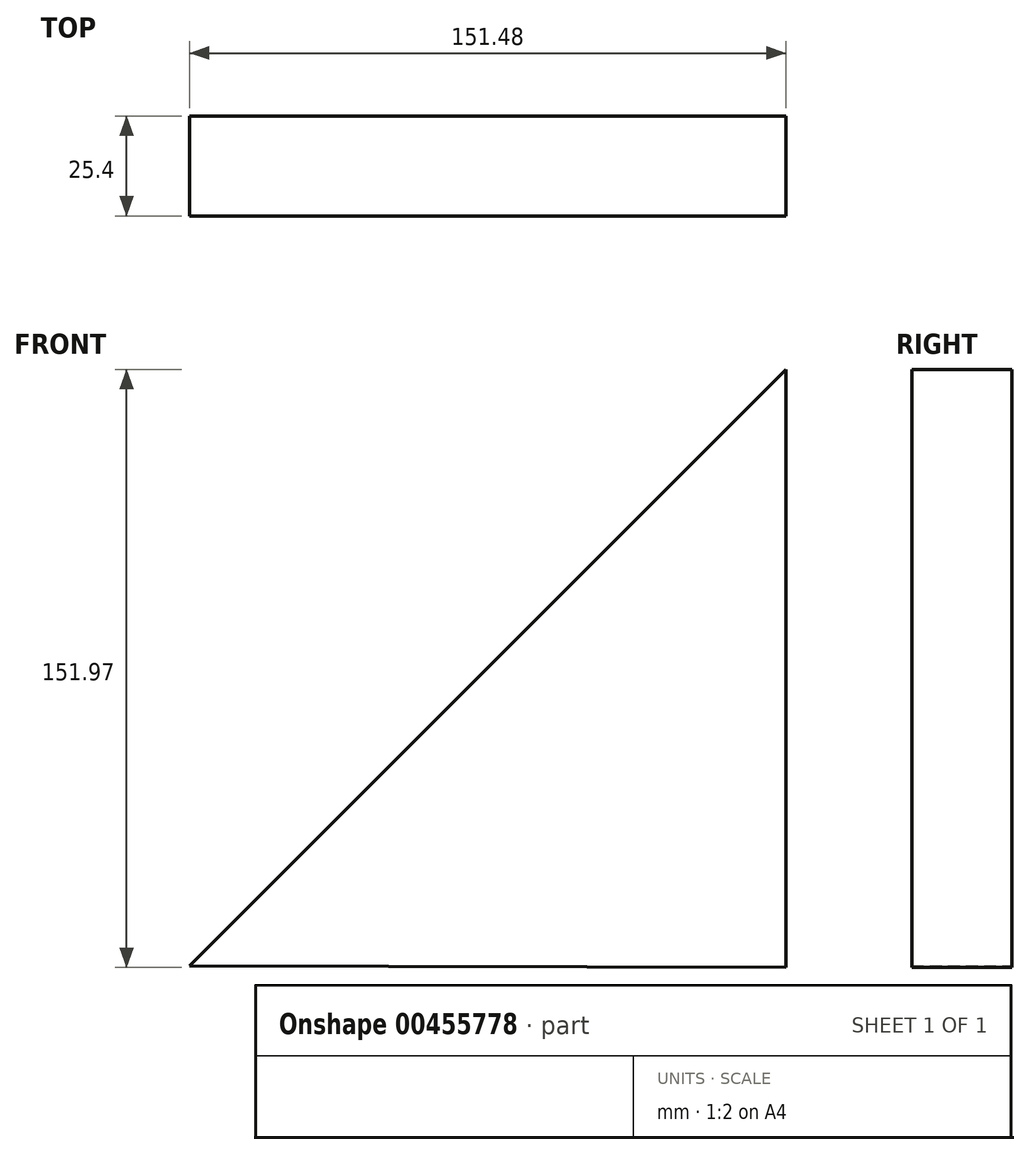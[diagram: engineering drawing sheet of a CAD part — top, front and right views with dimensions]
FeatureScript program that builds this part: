
annotation { "Feature Type Name" : "Feature", "Feature Type Description" : "" }
export const myFeature = defineFeature(function(context is Context, id is Id, definition is map)
    precondition{}
    {
        {
            var Q0;
            Q0=qCreatedBy(makeId("Front.planeOp"),FACE);
            var sketch = newSketch(context, id + "F0", { "sketchPlane" : qUnion([Q0])});
            skLineSegment(sketch, "E0", {"start": v(-75.86, -76.35) * mm, "end": v(75.62, 75.13) * mm});
            skLineSegment(sketch, "E1", {"start": v(75.62, 75.13) * mm, "end": v(75.62, -76.84) * mm});
            skLineSegment(sketch, "E2", {"start": v(75.62, -76.84) * mm, "end": v(-75.86, -76.35) * mm});
            skSolve(sketch);
        }
        {
            var Q0;
            Q0 = qSketchRegion(id + "F0", true);
            extrude(context, id + "F1", {"entities" : qUnion([Q0]), "depth" : 25.4 * mm});
        }
    });
